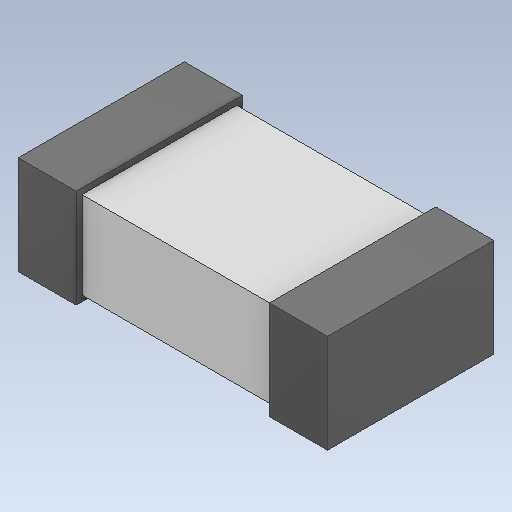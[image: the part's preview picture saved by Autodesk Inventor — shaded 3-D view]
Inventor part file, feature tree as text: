
AUTODESK INVENTOR PART (.ipt)
format: ipt  version: 2020 (Build 240168000, 168)  size: 100,352 bytes
history: native  units: mm
features: other x1, extrude x1
ambient origin geometry x8: Origin, YZ Plane, XZ Plane, XY Plane, X Axis, Y Axis, Z Axis, Center Point
bodies: Body1 (feature_tree)
feature tree (2):
  other  "Твердое тело1"
  extrude  "Extrude2"  [1 undecoded]
note: 1 required parameter value undecoded (feature->parameter linkage not recoverable at this tier; creation-order binding heuristic only, values carry confidence <= 0.55)
